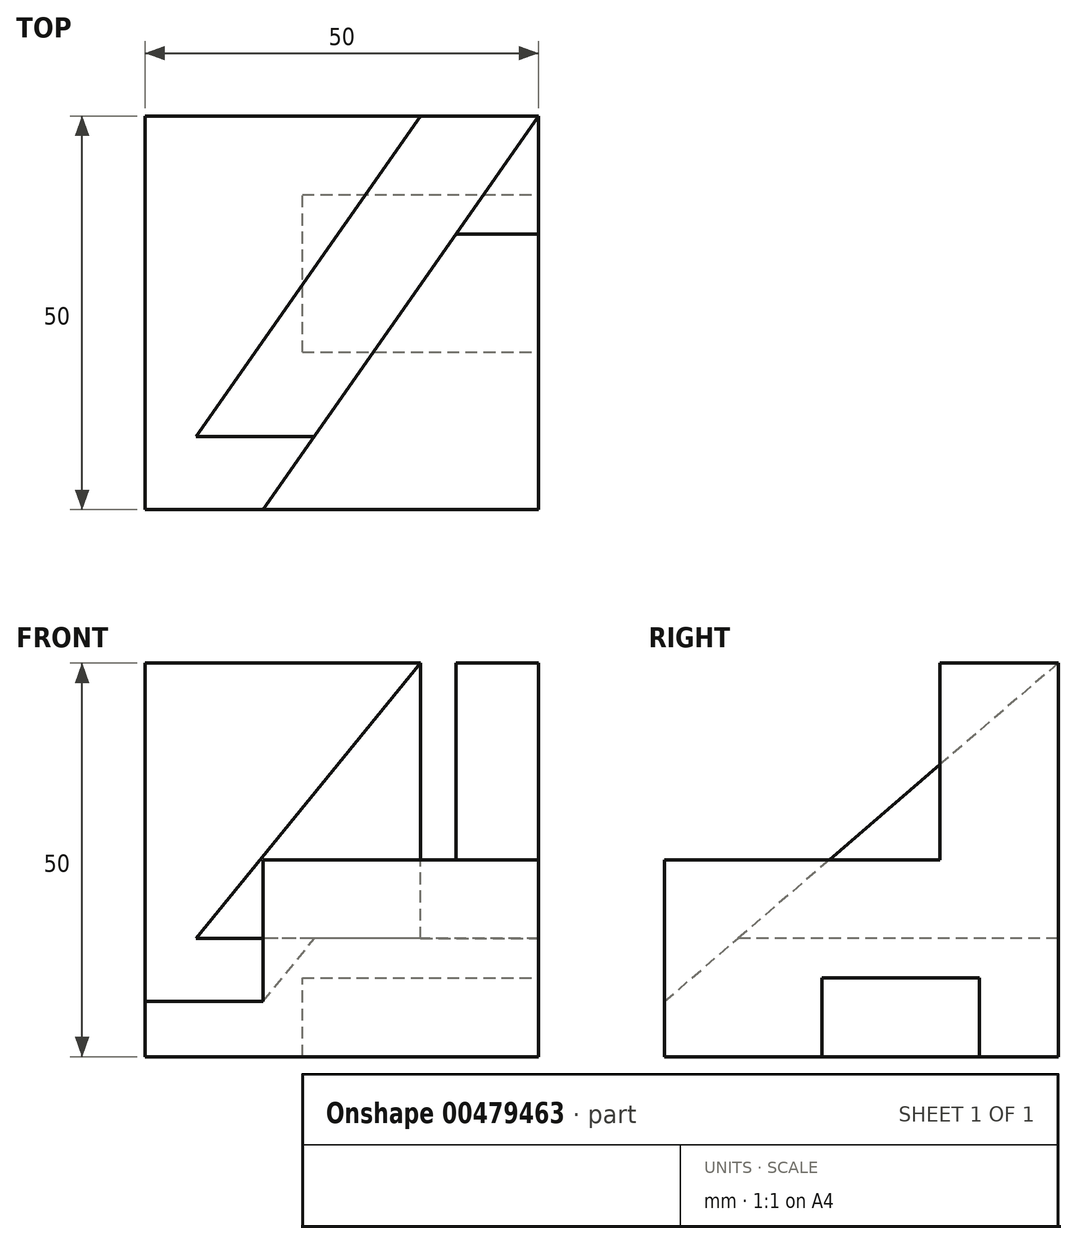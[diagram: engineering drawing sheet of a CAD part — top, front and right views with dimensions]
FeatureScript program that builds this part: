
annotation { "Feature Type Name" : "Feature", "Feature Type Description" : "" }
export const myFeature = defineFeature(function(context is Context, id is Id, definition is map)
    precondition{}
    {
        {
            var Q0;
            Q0=qCreatedBy(makeId("Top.planeOp"),FACE);
            var sketch = newSketch(context, id + "F0", { "sketchPlane" : qUnion([Q0])});
            skLineSegment(sketch, "E0.bottom", {"start": v(0, 0) * mm, "end": v(50, 0) * mm});
            skLineSegment(sketch, "E0.top", {"start": v(0, 50) * mm, "end": v(50, 50) * mm});
            skLineSegment(sketch, "E0.left", {"start": v(0, 0) * mm, "end": v(0, 50) * mm});
            skLineSegment(sketch, "E0.right", {"start": v(50, 0) * mm, "end": v(50, 50) * mm});
            skSolve(sketch);
        }
        {
            var Q0;
            Q0 = qSketchRegion(id + "F0", true);
            extrude(context, id + "F1", {"entities" : qUnion([Q0]), "depth" : 50 * mm});
        }
        {
            var Q0;
            Q0=makeQuery(id+"F1.opExtrude","SWEPT_FACE",FACE,{"disambiguationData":[OSD([sQuery(id+"F0.wireOp",EDGE,"E0.right")])]});
            var sketch = newSketch(context, id + "F2", { "sketchPlane" : qUnion([Q0])});
            skLineSegment(sketch, "E1", {"start": v(0, 0) * mm, "end": v(20, 0) * mm});
            skLineSegment(sketch, "E2", {"start": v(20, 0) * mm, "end": v(40, 0) * mm});
            skLineSegment(sketch, "E3", {"start": v(40, 0) * mm, "end": v(40, 10) * mm});
            skLineSegment(sketch, "E4", {"start": v(40, 10) * mm, "end": v(20, 10) * mm});
            skLineSegment(sketch, "E5", {"start": v(20, 0) * mm, "end": v(20, 10) * mm});
            skSolve(sketch);
        }
        {
            var Q0;
            Q0 = qSketchRegion(id + "F2", true);
            extrude(context, id + "F3", {"entities" : qUnion([Q0]), "operationType" : NewBodyOperationType.REMOVE, "oppositeDirection" : true, "depth" : 30 * mm});
        }
        {
            var Q0;
            Q0=makeQuery(id+"F1.opExtrude","SWEPT_FACE",FACE,{"disambiguationData":[OSD([sQuery(id+"F0.wireOp",EDGE,"E0.bottom")])]});
            var sketch = newSketch(context, id + "F4", { "sketchPlane" : qUnion([Q0])});
            skLineSegment(sketch, "E6", {"start": v(0, 0) * mm, "end": v(0, 7) * mm});
            skSolve(sketch);
        }
        {
            var Q0;
            {var subQ3=sQuery(id+"F4.wireOp",EDGE,"E6");Q0=makeQuery(id+"F4.imprint","IMPRINT",FACE,{"disambiguationData":[TD([[makeQuery(id+"F4.imprint","IMPRINT",EDGE,{"derivedFrom":subQ3}),1.0]])]});}
            var sketch = newSketch(context, id + "F5", { "sketchPlane" : qUnion([Q0])});
            skLineSegment(sketch, "E7", {"start": v(0, 0) * mm, "end": v(50, 0) * mm});
            skLineSegment(sketch, "E8", {"start": v(50, 0) * mm, "end": v(50, 25) * mm});
            skLineSegment(sketch, "E9", {"start": v(50, 25) * mm, "end": v(15, 25) * mm});
            skLineSegment(sketch, "E10", {"start": v(15, 7) * mm, "end": v(15, 25) * mm});
            skLineSegment(sketch, "E11", {"start": v(15, 7) * mm, "end": v(0, 7) * mm});
            skSolve(sketch);
        }
        {
            var Q0;
            Q0=makeQuery(id+"F1.opExtrude","SWEPT_FACE",FACE,{"disambiguationData":[OSD([sQuery(id+"F0.wireOp",EDGE,"E0.right")])]});
            var sketch = newSketch(context, id + "F6", { "sketchPlane" : qUnion([Q0])});
            skLineSegment(sketch, "E12", {"start": v(0, 25) * mm, "end": v(35, 25) * mm});
            skLineSegment(sketch, "E13", {"start": v(35, 25) * mm, "end": v(35, 50) * mm});
            skSolve(sketch);
        }
        {
            var Q0;
            Q0=makeQuery(id+"F1.opExtrude","CAP_FACE",FACE,{"disambiguationData":[OSD([sQuery(id+"F0.wireOp",EDGE,"E0.bottom"),sQuery(id+"F0.wireOp",EDGE,"E0.top"),sQuery(id+"F0.wireOp",EDGE,"E0.left"),sQuery(id+"F0.wireOp",EDGE,"E0.right")])],"isStart":false});
            var sketch = newSketch(context, id + "F7", { "sketchPlane" : qUnion([Q0])});
            skLineSegment(sketch, "E14", {"start": v(50, 50) * mm, "end": v(35, 50) * mm});
            skLineSegment(sketch, "E15", {"start": v(0, 0) * mm, "end": v(15, 0) * mm});
            skLineSegment(sketch, "E16", {"start": v(50, 50) * mm, "end": v(15, 0) * mm});
            skLineSegment(sketch, "E17", {"start": v(35, 50) * mm, "end": v(0, 0) * mm});
            skSolve(sketch);
        }
        {
            var Q0;
            Q0=makeQuery(id+"F7.imprint","IMPRINT",FACE,{"disambiguationData":[TD([[makeQuery(id+"F7.imprint","IMPRINT",EDGE,{"derivedFrom":sQuery(id+"F7.wireOp",EDGE,"E14")}),-1.0]])]});
            extrude(context, id + "F8", {"entities" : qUnion([Q0]), "operationType" : NewBodyOperationType.REMOVE, "oppositeDirection" : true, "depth" : 35 * mm});
        }
        {
            var Q0;
            {var subQ0=sQuery(id+"F0.wireOp",EDGE,"E0.bottom");var subQ1=sQuery(id+"F0.wireOp",EDGE,"E0.right");Q0=makeQuery(id+"F8.boolean.opBoolean","SPLIT",FACE,{"disambiguationData":[TD([makeQuery(id+"F1.opExtrude","SWEPT_FACE",FACE,{"disambiguationData":[OSD([subQ0])]})])],"derivedFrom":makeQuery(id+"F1.opExtrude","CAP_FACE",FACE,{"disambiguationData":[OSD([subQ0,sQuery(id+"F0.wireOp",EDGE,"E0.top"),sQuery(id+"F0.wireOp",EDGE,"E0.left"),subQ1])],"isStart":false})});}
            var sketch = newSketch(context, id + "F9", { "sketchPlane" : qUnion([Q0])});
            skLineSegment(sketch, "E18", {"start": v(50, 0) * mm, "end": v(50, 35) * mm});
            skLineSegment(sketch, "E19", {"start": v(50, 35) * mm, "end": v(39.5, 35) * mm});
            skSolve(sketch);
        }
        {
            var Q0;
            Q0=makeQuery(id+"F9.imprint","IMPRINT",FACE,{"disambiguationData":[TD([[makeQuery(id+"F9.imprint","IMPRINT",EDGE,{"derivedFrom":sQuery(id+"F9.wireOp",EDGE,"E18")}),1.0]])]});
            extrude(context, id + "F10", {"entities" : qUnion([Q0]), "operationType" : NewBodyOperationType.REMOVE, "oppositeDirection" : true, "depth" : 25 * mm});
        }
        {
            var Q0;
            Q0=makeQuery(id+"F1.opExtrude","SWEPT_FACE",FACE,{"disambiguationData":[OSD([sQuery(id+"F0.wireOp",EDGE,"E0.left")])]});
            var sketch = newSketch(context, id + "F11", { "sketchPlane" : qUnion([Q0])});
            skLineSegment(sketch, "E20", {"start": v(-50, 50) * mm, "end": v(0, 7) * mm});
            skLineSegment(sketch, "E21", {"start": v(0, 7) * mm, "end": v(0, 50) * mm});
            skLineSegment(sketch, "E22", {"start": v(-50, 50) * mm, "end": v(0, 50) * mm});
            skSolve(sketch);
        }
        {
            var Q0;
            Q0 = qSketchRegion(id + "F11", true);
            var Q1;
            Q1=makeQuery(id+"F8.boolean.opBoolean","COPY",FACE,{"derivedFrom":makeQuery(id+"F8.opExtrude","SWEPT_FACE",FACE,{"disambiguationData":[OSD([sQuery(id+"F7.wireOp",EDGE,"E16")])]})});
            extrude(context, id + "F12", {"entities" : qUnion([Q0]), "operationType" : NewBodyOperationType.REMOVE, "endBound" : BoundingType.UP_TO_SURFACE, "oppositeDirection" : true, "depth" : 25 * mm, "endBoundEntityFace" : qUnion([Q1]), "offsetDistance" : 25 * mm});
        }
    });
